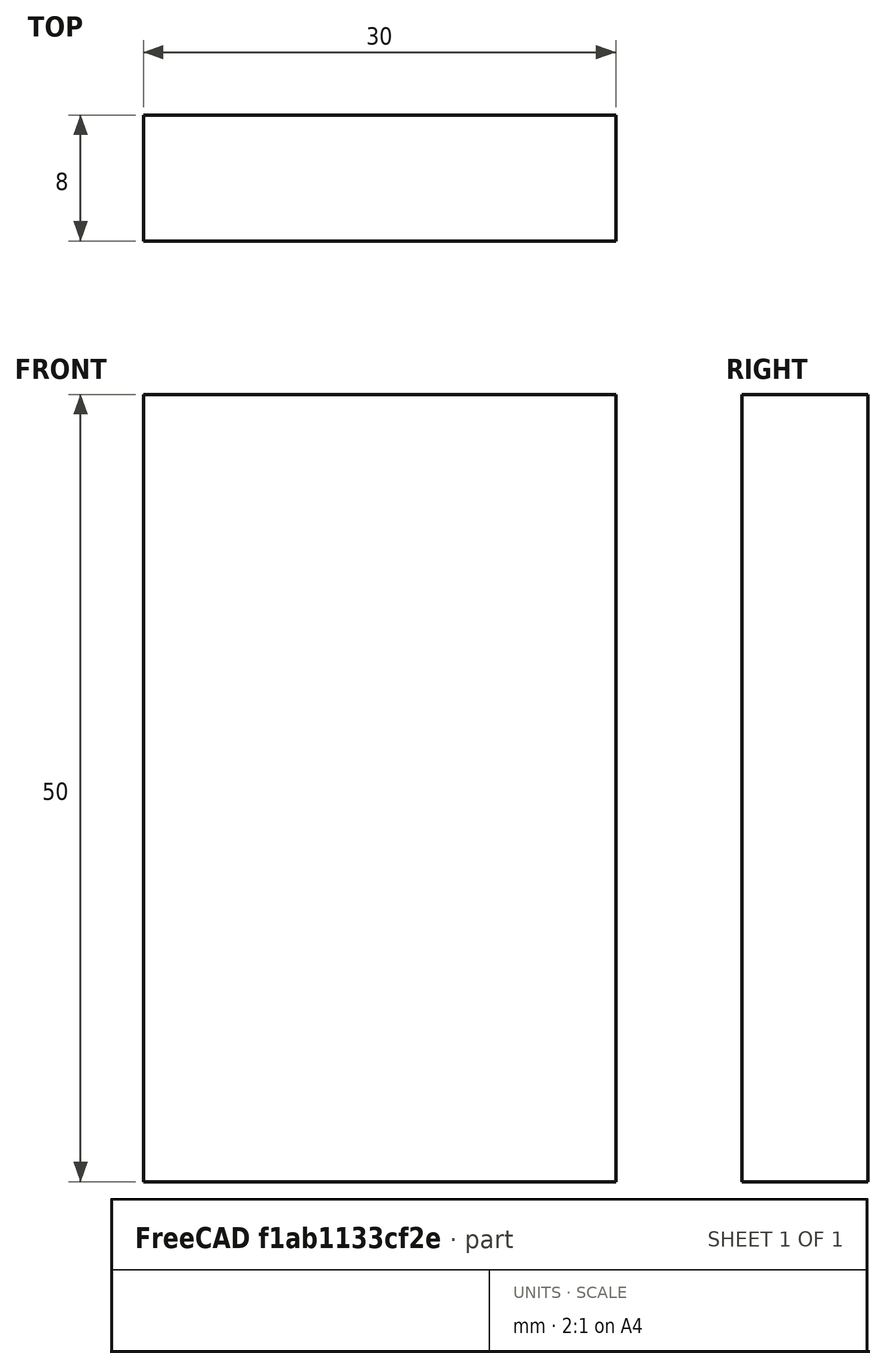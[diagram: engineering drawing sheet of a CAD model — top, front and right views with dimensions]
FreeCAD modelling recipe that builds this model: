
FCSTD DOCUMENT  (FreeCAD 0.15R4671 (Git))
Label: Flat Bar 30x8 EN10058 S235JR
License: All rights reserved
LicenseURL: http://en.wikipedia.org/wiki/All_rights_reserved
objects: Sketcher::SketchObject×1, Part::Extrusion×1
note: 2 computed .brp shape members not serialized (recipe doc carries the construction recipe); baked Part::Feature solids carry a one-line shape summary decoded from their .brp

FEATURE [Sketcher::SketchObject] Sketch
  sketch-geometry (4):
    g0: LineSegment StartX=-15 StartY=-4 StartZ=0 EndX=15 EndY=-4 EndZ=0
    g1: LineSegment StartX=15 StartY=-4 StartZ=0 EndX=15 EndY=4 EndZ=0
    g2: LineSegment StartX=15 StartY=4 StartZ=0 EndX=-15 EndY=4 EndZ=0
    g3: LineSegment StartX=-15 StartY=4 StartZ=0 EndX=-15 EndY=-4 EndZ=0
  constraints (12):
    c: Coincident(g0,g1)
    c: Coincident(g1,g2)
    c: Coincident(g2,g3)
    c: Coincident(g3,g0)
    c: Horizontal(g0)
    c: Horizontal(g2)
    c: Vertical(g1)
    c: Vertical(g3)
    c: Symmetric(g1,g2,g-2)
    c: Symmetric(g0,g1,g-1)
    c: DistanceY(g1) = 8
    c: DistanceX(g0) = 30
FEATURE [Part::Extrusion] Extrude  label="Flat Bar 30x8 EN10058 S235JR"
  Base = -> Sketch
  Dir = (0,0,50)
  Solid = true
